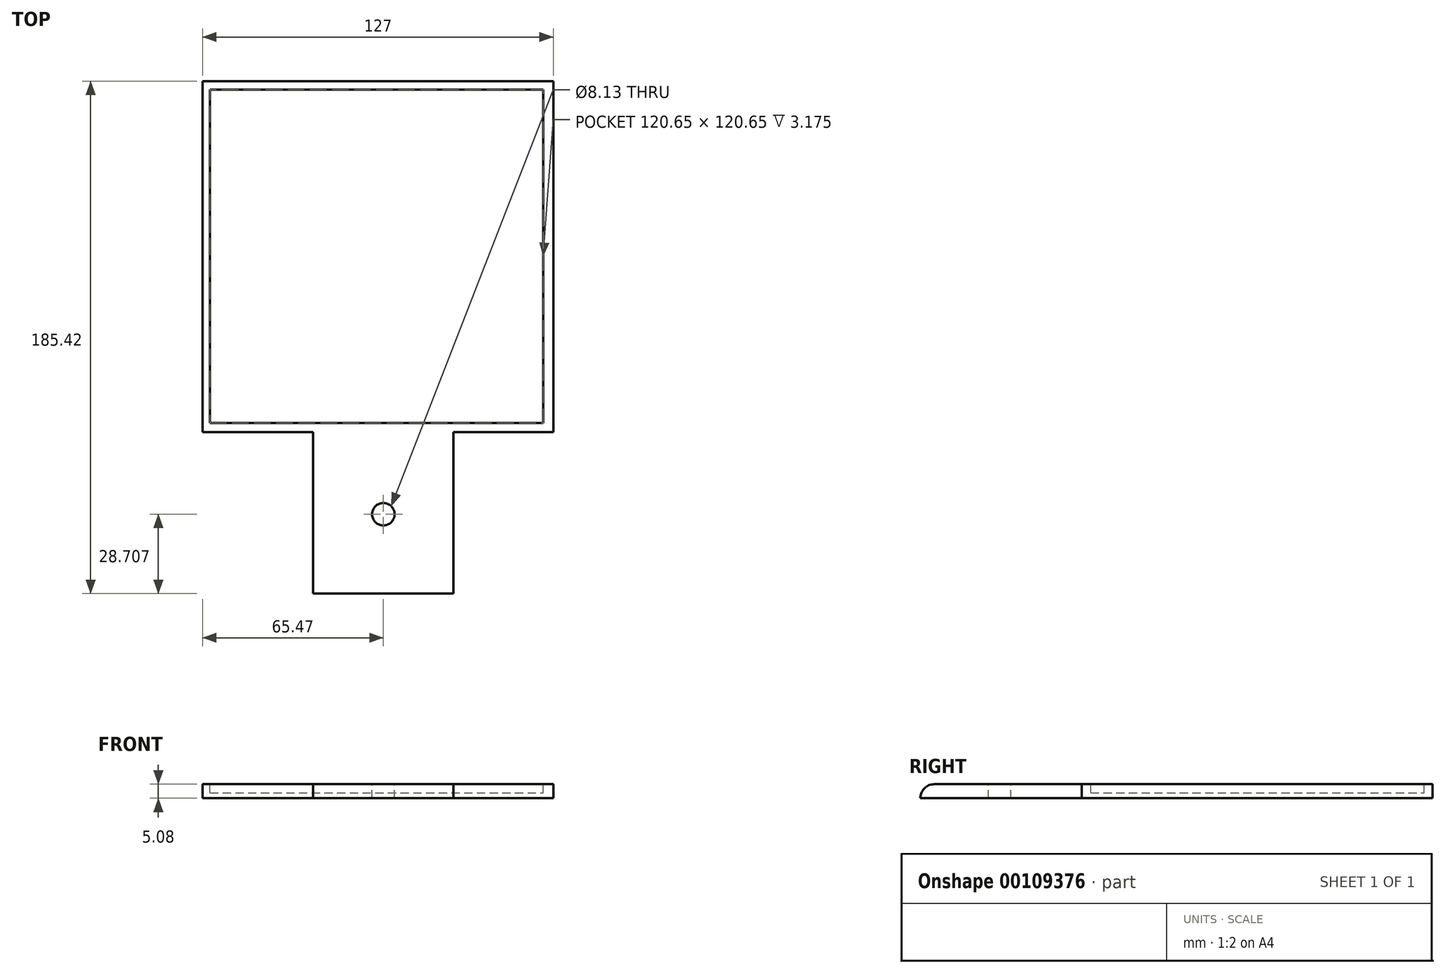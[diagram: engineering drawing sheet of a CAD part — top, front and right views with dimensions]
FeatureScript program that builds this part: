
annotation { "Feature Type Name" : "Feature", "Feature Type Description" : "" }
export const myFeature = defineFeature(function(context is Context, id is Id, definition is map)
    precondition{}
    {
        {
            var Q0;
            Q0=qCreatedBy(makeId("Top.planeOp"),FACE);
            var sketch = newSketch(context, id + "F0", { "sketchPlane" : qUnion([Q0])});
            skLineSegment(sketch, "E0.bottom", {"start": v(-65.47, -66.93) * mm, "end": v(61.53, -66.93) * mm});
            skLineSegment(sketch, "E0.top", {"start": v(-65.47, 60.07) * mm, "end": v(61.53, 60.07) * mm});
            skLineSegment(sketch, "E0.left", {"start": v(-65.47, -66.93) * mm, "end": v(-65.47, 60.07) * mm});
            skLineSegment(sketch, "E0.right", {"start": v(61.53, -66.93) * mm, "end": v(61.53, 60.07) * mm});
            skSolve(sketch);
        }
        {
            var Q0;
            Q0=qCreatedBy(makeId("Top.planeOp"),FACE);
            var sketch = newSketch(context, id + "F1", { "sketchPlane" : qUnion([Q0])});
            skSolve(sketch);
        }
        {
            var Q0;
            Q0 = qSketchRegion(id + "F1", true);
            var Q1;
            Q1=makeQuery(id+"F0.imprint","IMPRINT",FACE,{"disambiguationData":[TD([[makeQuery(id+"F0.imprint","IMPRINT",EDGE,{"derivedFrom":sQuery(id+"F0.wireOp",EDGE,"E0.bottom")}),1.0]])]});
            extrude(context, id + "F2", {"entities" : qUnion([Q0, Q1]), "oppositeDirection" : true, "depth" : 5.08 * mm});
        }
        {
            var Q0;
            Q0=makeQuery(id+"F2.opExtrude","CAP_FACE",FACE,{"disambiguationData":[OSD([sQuery(id+"F0.wireOp",EDGE,"E0.bottom"),sQuery(id+"F0.wireOp",EDGE,"E0.top"),sQuery(id+"F0.wireOp",EDGE,"E0.left"),sQuery(id+"F0.wireOp",EDGE,"E0.right")])],"isStart":true});
            var sketch = newSketch(context, id + "F3", { "sketchPlane" : qUnion([Q0])});
            skLineSegment(sketch, "E1", {"start": v(-25.4, -66.93) * mm, "end": v(-25.4, -125.35) * mm});
            skLineSegment(sketch, "E2", {"start": v(-25.4, -125.35) * mm, "end": v(25.4, -125.35) * mm});
            skLineSegment(sketch, "E3.MirrorCS", {"start": v(25.4, -66.93) * mm, "end": v(25.4, -125.35) * mm});
            skLineSegment(sketch, "E4", {"start": v(-25.4, -96.14) * mm, "end": v(25.4, -96.14) * mm, "construction": true});
            skLineSegment(sketch, "E5", {"start": v(0, -125.35) * mm, "end": v(0, 109.5) * mm, "construction": true});
            skPoint(sketch, "E5.endSnap0", {"position": v(0, -96.14) * mm});
            skSolve(sketch);
        }
        {
            var Q0;
            {var subQ0=sQuery(id+"F3.wireOp",EDGE,"E1");Q0=makeQuery(id+"F3.imprint","IMPRINT",FACE,{"disambiguationData":[TD([[makeQuery(id+"F3.imprint","IMPRINT",EDGE,{"derivedFrom":subQ0}),1.0]])]});}
            extrude(context, id + "F4", {"entities" : qUnion([Q0]), "operationType" : NewBodyOperationType.ADD, "oppositeDirection" : true, "depth" : 5.08 * mm});
        }
        {
            var Q0;
            Q0=makeQuery(id+"F4.opExtrude","SWEPT_FACE",FACE,{"disambiguationData":[OSD([sQuery(id+"F3.wireOp",EDGE,"E2")])]});
            var sketch = newSketch(context, id + "F5", { "sketchPlane" : qUnion([Q0])});
            skLineSegment(sketch, "E6", {"start": v(25.4, -5.08) * mm, "end": v(25.4, -17.78) * mm});
            skLineSegment(sketch, "E7", {"start": v(-25.4, -5.08) * mm, "end": v(-25.4, -17.78) * mm});
            skLineSegment(sketch, "E8", {"start": v(-25.4, -17.78) * mm, "end": v(25.4, -17.78) * mm});
            skSolve(sketch);
        }
        {
            var Q0;
            Q0=makeQuery(id+"F5.imprint","IMPRINT",FACE,{"disambiguationData":[TD([[makeQuery(id+"F5.imprint","IMPRINT",EDGE,{"derivedFrom":sQuery(id+"F5.wireOp",EDGE,"E6")}),-1.0]])]});
            extrude(context, id + "F6", {"entities" : qUnion([Q0]), "operationType" : NewBodyOperationType.REMOVE, "oppositeDirection" : true, "depth" : 2.54 * mm});
        }
        {
            var Q0;
            Q0=makeQuery(id+"F4.opExtrude","CAP_EDGE",EDGE,{"disambiguationData":[OSD([sQuery(id+"F3.wireOp",EDGE,"E2")])],"isStart":true});
            fillet(context, id + "F7", {"entities" : qUnion([Q0]), "radius" : 5.08 * mm, "tangentPropagation" : true, "allowEdgeOverflow" : false});
        }
        {
            var Q0;
            {var subQ0=sQuery(id+"F0.wireOp",EDGE,"E0.bottom");Q0=makeQuery(id+"F4.boolean.opBoolean","MERGE",FACE,{"derivedFrom":[makeQuery(id+"F2.opExtrude","CAP_FACE",FACE,{"disambiguationData":[OSD([subQ0,sQuery(id+"F0.wireOp",EDGE,"E0.top"),sQuery(id+"F0.wireOp",EDGE,"E0.left"),sQuery(id+"F0.wireOp",EDGE,"E0.right")])],"isStart":true}),makeQuery(id+"F4.opExtrude","CAP_FACE",FACE,{"disambiguationData":[OSD([subQ0,sQuery(id+"F3.wireOp",EDGE,"E1"),sQuery(id+"F3.wireOp",EDGE,"E2"),sQuery(id+"F3.wireOp",EDGE,"E3.MirrorCS")])],"isStart":true})]});}
            var sketch = newSketch(context, id + "F8", { "sketchPlane" : qUnion([Q0])});
            skSolve(sketch);
        }
        {
            var Q0;
            Q0=qCreatedBy(makeId("Top.planeOp"),FACE);
            var sketch = newSketch(context, id + "F9", { "sketchPlane" : qUnion([Q0])});
            skLineSegment(sketch, "E9.bottom", {"start": v(-62.74, -63.67) * mm, "end": v(57.9, -63.67) * mm});
            skLineSegment(sketch, "E9.top", {"start": v(-62.74, 56.98) * mm, "end": v(57.9, 56.98) * mm});
            skLineSegment(sketch, "E9.left", {"start": v(-62.74, -63.67) * mm, "end": v(-62.74, 56.98) * mm});
            skLineSegment(sketch, "E9.right", {"start": v(57.9, -63.67) * mm, "end": v(57.9, 56.98) * mm});
            skSolve(sketch);
        }
        {
            var Q0;
            Q0 = qSketchRegion(id + "F9", true);
            extrude(context, id + "F10", {"entities" : qUnion([Q0]), "operationType" : NewBodyOperationType.REMOVE, "oppositeDirection" : true, "depth" : 3.17 * mm});
        }
        {
            var Q0;
            {var subQ3=sQuery(id+"F0.wireOp",EDGE,"E0.top");Q0=makeQuery(id+"F8.imprint","IMPRINT",FACE,{"disambiguationData":[TD([[makeQuery(id+"F8.imprint","IMPRINT",EDGE,{"derivedFrom":makeQuery(id+"F2.opExtrude","CAP_EDGE",EDGE,{"disambiguationData":[OSD([subQ3])],"isStart":true})}),-1.0]])]});}
            var sketch = newSketch(context, id + "F11", { "sketchPlane" : qUnion([Q0])});
            skCircle(sketch, "E10", {"center": v(0, -96.64) * mm, "radius": 4.06 * mm});
            skLineSegment(sketch, "E11", {"start": v(0, -128.62) * mm, "end": v(0, 73.01) * mm, "construction": true});
            skLineSegment(sketch, "E12", {"start": v(-36.94, -96.64) * mm, "end": v(37.29, -96.64) * mm, "construction": true});
            skSolve(sketch);
        }
        {
            var Q0;
            Q0 = qSketchRegion(id + "F11", true);
            extrude(context, id + "F12", {"entities" : qUnion([Q0]), "operationType" : NewBodyOperationType.REMOVE, "oppositeDirection" : true, "depth" : 25.4 * mm});
        }
    });
